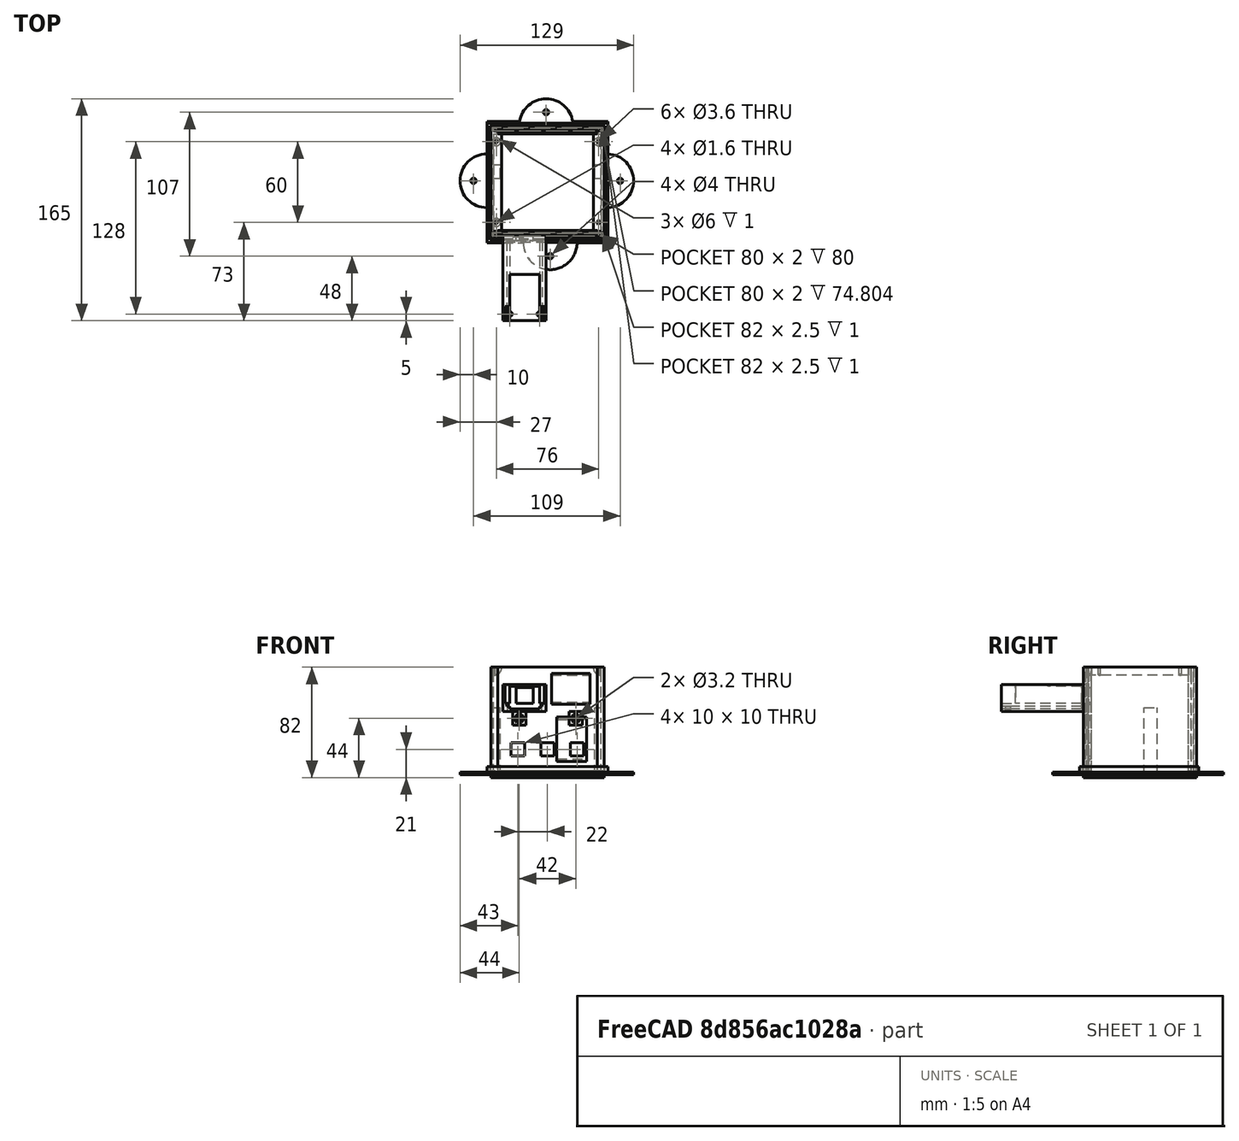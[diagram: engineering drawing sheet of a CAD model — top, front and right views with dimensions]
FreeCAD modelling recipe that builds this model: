
FCSTD DOCUMENT  (FreeCAD 0.19R24291 (Git))
Label: Project_ELE1
License: All rights reserved
LicenseURL: http://en.wikipedia.org/wiki/All_rights_reserved
objects: Part::Box×31, Part::Cylinder×25, Part::MultiFuse×9, Part::Cut×8, Part::Thickness×2, Part::FeaturePython×2, App::MeasureDistance×1
note: 77 computed .brp shape members not serialized (recipe doc carries the construction recipe); baked Part::Feature solids carry a one-line shape summary decoded from their .brp

FEATURE [Part::Box] Box  label="Cube"
  AttacherType = Attacher::AttachEngine3D
  Height = 80
  Length = 80
  Width = 80
FEATURE [Part::Thickness] Thickness
  Faces = -> Box [Face6]
  Intersection = false
  Join = 2
  Mode = 0
  SelfIntersection = false
  Value = 2
FEATURE [Part::Box] Box001  label="Cube001"
  AttacherType = Attacher::AttachEngine3D
  Height = 80
  Length = 80
  Placement = pos=(0,2,0) rot=(0,0,1;0rad)
  Width = 2
FEATURE [Part::Box] Box002  label="Cube002"
  AttacherType = Attacher::AttachEngine3D
  Height = 77
  Length = 74
  Placement = pos=(3,-4,3) rot=(0,0,1;0rad)
  Width = 8
FEATURE [Part::Cylinder] Cylinder
  Angle = 360
  AttacherType = Attacher::AttachEngine3D
  Height = 10
  Placement = pos=(2,10,70) rot=(0,0,1;0rad)
  Radius = 0.8
FEATURE [Part::Cylinder] Cylinder001
  Angle = 360
  AttacherType = Attacher::AttachEngine3D
  Height = 10
  Placement = pos=(2,70,70) rot=(0,0,1;0rad)
  Radius = 0.8
FEATURE [Part::Cylinder] Cylinder002
  Angle = 360
  AttacherType = Attacher::AttachEngine3D
  Height = 10
  Placement = pos=(78,70,70) rot=(0,0,1;0rad)
  Radius = 0.8
FEATURE [Part::Cylinder] Cylinder003
  Angle = 360
  AttacherType = Attacher::AttachEngine3D
  Height = 10
  Placement = pos=(78,10,70) rot=(0,0,1;0rad)
  Radius = 0.8
FEATURE [Part::Box] Box003  label="Cube003"
  AttacherType = Attacher::AttachEngine3D
  Height = 80
  Length = 80
  Placement = pos=(0,76,0) rot=(0,0,1;0rad)
  Width = 2
FEATURE [Part::Box] Box004  label="Cube004"
  AttacherType = Attacher::AttachEngine3D
  Height = 77
  Length = 74
  Placement = pos=(3,76,3) rot=(0,0,1;0rad)
  Width = 9
FEATURE [Part::MultiFuse] Fusion001
  Shapes = -> [Box002,Cylinder,Cylinder001,Cylinder002,Cylinder003,Box004]
FEATURE [Part::Cylinder] Cylinder004
  Angle = 90
  AttacherType = Attacher::AttachEngine3D
  Height = 74
  Placement = pos=(0,78,80) rot=(0.57735,0.57735,-0.57735;2.0944rad)
  Radius = 6
FEATURE [Part::Cylinder] Cylinder005
  Angle = 90
  AttacherType = Attacher::AttachEngine3D
  Height = 74
  Placement = pos=(80,78,80) rot=(0,0.707107,-0.707107;3.14159rad)
  Radius = 6
FEATURE [Part::Box] Box005  label="Cube005"
  AttacherType = Attacher::AttachEngine3D
  Height = 50
  Length = 5
  Placement = pos=(0,43,0) rot=(0,0,1;0rad)
  Width = 10
FEATURE [Part::Box] Box006  label="Cube006"
  AttacherType = Attacher::AttachEngine3D
  Height = 50
  Length = 5
  Placement = pos=(75,43,0) rot=(0,0,1;0rad)
  Width = 10
FEATURE [Part::MultiFuse] Fusion
  Shapes = -> [Box001,Thickness,Box003,Cylinder004,Cylinder005,Box005,Box006]
FEATURE [Part::Cut] Cut  label="Cut_obal"
  Base = -> Fusion
  Tool = -> Fusion001
FEATURE [Part::Box] Box007  label="Cube007"
  AttacherType = Attacher::AttachEngine3D
  Height = 77
  Length = 74
  Placement = pos=(3,1,3) rot=(0,0,1;0rad)
  Width = 2
FEATURE [Part::Box] Box008  label="Cube008"
  AttacherType = Attacher::AttachEngine3D
  Height = 79.5
  Length = 80
  Placement = pos=(0,2,0.5) rot=(0,0,1;0rad)
  Width = 1.5
FEATURE [Part::Cylinder] Cylinder006
  Angle = 360
  AttacherType = Attacher::AttachEngine3D
  Height = 10
  Placement = pos=(19,4,42) rot=(1,0,0;1.5708rad)
  Radius = 1.6
FEATURE [Part::Cylinder] Cylinder007
  Angle = 360
  AttacherType = Attacher::AttachEngine3D
  Height = 10
  Placement = pos=(61,5,42) rot=(1,0,0;1.5708rad)
  Radius = 1.6
FEATURE [Part::FeaturePython] Nut  label="(M3.5)-Nut"  # Fasteners workbench fastener (typed FeaturePython)
  Placement = pos=(19,1,42) rot=(1,0,0;1.5708rad)
  diameter = 5
  invert = false
  matchOuter = false
  offset = 0
  thread = false
  type = 9
FEATURE [Part::FeaturePython] Nut001  label="(M3.5)-Nut001"  # Fasteners workbench fastener (typed FeaturePython)
  Placement = pos=(61,1,42) rot=(1,0,0;1.5708rad)
  diameter = 5
  invert = false
  matchOuter = false
  offset = 0
  thread = false
  type = 9
FEATURE [Part::Box] Box009  label="Cube009"
  AttacherType = Attacher::AttachEngine3D
  Height = 10
  Length = 10
  Placement = pos=(14,-0.5,37) rot=(0,0,1;0rad)
  Width = 2
FEATURE [Part::Box] Box010  label="Cube010"
  AttacherType = Attacher::AttachEngine3D
  Height = 10
  Length = 10
  Placement = pos=(56,-0.5,37) rot=(0,0,1;0rad)
  Width = 4
FEATURE [Part::Box] Box012  label="Cube012"
  AttacherType = Attacher::AttachEngine3D
  Height = 10
  Length = 10
  Placement = pos=(13,0,14) rot=(0,0,1;0rad)
  Width = 10
FEATURE [Part::Box] Box013  label="Cube013"
  AttacherType = Attacher::AttachEngine3D
  Height = 10
  Length = 10
  Placement = pos=(57,0,14) rot=(0,0,1;0rad)
  Width = 10
FEATURE [Part::MultiFuse] Fusion003
  Shapes = -> [Box007,Box008,Box009,Box010]
FEATURE [Part::Box] Box014  label="Cube014"
  AttacherType = Attacher::AttachEngine3D
  Height = 79.5
  Length = 80
  Placement = pos=(0,2,0.5) rot=(0,0,1;0rad)
  Width = 1.5
FEATURE [Part::Box] Box015  label="Cube015"
  AttacherType = Attacher::AttachEngine3D
  Height = 77
  Length = 74
  Placement = pos=(3,1,3) rot=(0,0,1;0rad)
  Width = 2
FEATURE [Part::Box] Box018  label="Vypinac"
  AttacherType = Attacher::AttachEngine3D
  Height = 29
  Length = 22
  Placement = pos=(47,-6.5,12) rot=(0,0,1;0rad)
  Width = 10
FEATURE [Part::Box] Box019  label="PC"
  AttacherType = Attacher::AttachEngine3D
  Height = 20
  Length = 28.5
  Placement = pos=(43,0,54) rot=(0,0,1;0rad)
  Width = 10
FEATURE [Part::Box] Box020  label="Vypinac001"
  AttacherType = Attacher::AttachEngine3D
  Height = 33
  Length = 22
  Placement = pos=(47,-7.5,10) rot=(0,0,1;0rad)
  Width = 10
FEATURE [Part::Box] Box021  label="PC001"
  AttacherType = Attacher::AttachEngine3D
  Height = 23
  Length = 28.5
  Placement = pos=(43,-7.3,52.5) rot=(0,0,1;0rad)
  Width = 10
FEATURE [Part::Box] Box022  label="Cube016_USB"
  AttacherType = Attacher::AttachEngine3D
  Height = 12
  Length = 12.6
  Placement = pos=(16.7,-9,53) rot=(0,0,1;0rad)
  Width = 20
FEATURE [Part::Box] Box023  label="Cube017_rele"
  AttacherType = Attacher::AttachEngine3D
  Height = 20
  Length = 32
  Placement = pos=(39,1,47) rot=(0,0,1;3.14159rad)
  Width = 64
FEATURE [Part::MultiFuse] Fusion005
  Shapes = -> [Box015,Box014,Box023]
FEATURE [Part::Box] Box024  label="Cube018_doska"
  AttacherType = Attacher::AttachEngine3D
  Height = 2.2
  Length = 26.2
  Placement = pos=(35.9,-3.5,51) rot=(0,0,1;3.14159rad)
  Width = 60
FEATURE [Part::Box] Box025  label="Cube019_okolo_doskjy"
  AttacherType = Attacher::AttachEngine3D
  Height = 17
  Length = 22
  Placement = pos=(34,-3.5,49) rot=(0,0,1;3.14159rad)
  Width = 60
FEATURE [Part::Cylinder] Cylinder008
  Angle = 360
  AttacherType = Attacher::AttachEngine3D
  Height = 30
  Placement = pos=(34,-58,38) rot=(0,0,1;0rad)
  Radius = 1.8
FEATURE [Part::Cylinder] Cylinder009
  Angle = 360
  AttacherType = Attacher::AttachEngine3D
  Height = 30
  Placement = pos=(12,-58,38) rot=(0,0,1;0rad)
  Radius = 1.8
FEATURE [Part::Box] Box026  label="Cube016_pre_sroby"
  AttacherType = Attacher::AttachEngine3D
  Height = 15
  Length = 29
  Placement = pos=(8.5,-65.5,53.2) rot=(0,0,1;0rad)
  Width = 13
FEATURE [Part::Box] Box027  label="Cube016_pre_rele"
  AttacherType = Attacher::AttachEngine3D
  Height = 15
  Length = 22
  Placement = pos=(12,-53.5,65.2) rot=(0,0,1;0rad)
  Width = 25
FEATURE [Part::MultiFuse] Fusion006  label="Fusion006_usbrele"
  Shapes = -> [Box022,Box024,Box025,Cylinder008,Cylinder009,Box026,Box027]
FEATURE [Part::MultiFuse] Fusion004
  Shapes = -> [Box018,Box019,Box020,Box021,Fusion006]
FEATURE [Part::Cut] Cut002  label="Cut_zadok_usb"
  Base = -> Fusion005
  Tool = -> Fusion004
FEATURE [Part::Box] Box028  label="Cube016"
  AttacherType = Attacher::AttachEngine3D
  Height = 10
  Length = 10
  Placement = pos=(35,0,14) rot=(0,0,1;0rad)
  Width = 10
FEATURE [Part::MultiFuse] Fusion002
  Shapes = -> [Cylinder006,Cylinder007,Nut,Nut001,Box013,Box012,Box028]
FEATURE [Part::Cut] Cut001  label="Cut_predok"
  Base = -> Fusion003
  Tool = -> Fusion002
FEATURE [Part::Box] Box029  label="Cube017"
  AttacherType = Attacher::AttachEngine3D
  Height = 2
  Length = 90
  Placement = pos=(-5,-5,0) rot=(0,0,1;0rad)
  Width = 90
FEATURE [Part::Box] Box030  label="Cube018"
  AttacherType = Attacher::AttachEngine3D
  Height = 1
  Length = 82
  Placement = pos=(-1,0,1) rot=(0,0,1;0rad)
  Width = 2.5
FEATURE [Part::Cylinder] Cylinder012
  Angle = 360
  AttacherType = Attacher::AttachEngine3D
  Height = 300
  Placement = pos=(78,10,-70) rot=(0,0,1;0rad)
  Radius = 1.8
FEATURE [Part::Cylinder] Cylinder013
  Angle = 360
  AttacherType = Attacher::AttachEngine3D
  Height = 300
  Placement = pos=(78,70,-107) rot=(0,0,1;0rad)
  Radius = 1.8
FEATURE [Part::Cylinder] Cylinder014
  Angle = 360
  AttacherType = Attacher::AttachEngine3D
  Height = 300
  Placement = pos=(2,10,-63) rot=(0,0,1;0rad)
  Radius = 1.8
FEATURE [Part::Cylinder] Cylinder015
  Angle = 360
  AttacherType = Attacher::AttachEngine3D
  Height = 300
  Placement = pos=(2,70,-69) rot=(0,0,1;0rad)
  Radius = 1.8
FEATURE [Part::Box] Box034  label="Cube022"
  AttacherType = Attacher::AttachEngine3D
  Height = 1
  Length = 82
  Placement = pos=(-1,78,1) rot=(0,0,1;0rad)
  Width = 2.5
FEATURE [Part::Box] Box035  label="Cube023"
  AttacherType = Attacher::AttachEngine3D
  Height = 2
  Length = 84
  Placement = pos=(-2,-4,1) rot=(0,0,1;0rad)
  Width = 2
FEATURE [Part::Box] Box038  label="Cube026"
  AttacherType = Attacher::AttachEngine3D
  Height = 4
  Length = 85.6
  Placement = pos=(-2.8,-2.8,2) rot=(0,0,1;0rad)
  Width = 84.6
FEATURE [Part::Thickness] Thickness001
  Faces = -> Box038 [Face5,Face6]
  Intersection = false
  Join = 2
  Mode = 0
  SelfIntersection = false
  Value = 2
FEATURE [Part::Cylinder] Cylinder016
  Angle = 360
  AttacherType = Attacher::AttachEngine3D
  Height = 1
  Placement = pos=(2,10,0) rot=(0,0,1;0rad)
  Radius = 3
FEATURE [Part::Cylinder] Cylinder017
  Angle = 360
  AttacherType = Attacher::AttachEngine3D
  Height = 1
  Placement = pos=(2,70,0) rot=(0,0,1;0rad)
  Radius = 3
FEATURE [Part::Cylinder] Cylinder018
  Angle = 360
  AttacherType = Attacher::AttachEngine3D
  Height = 1
  Placement = pos=(78,70,0) rot=(0,0,1;0rad)
  Radius = 3
FEATURE [Part::MultiFuse] Fusion008
  Shapes = -> [Cylinder014,Cylinder015,Cylinder013,Cylinder012,Box034,Box030,Cylinder016,Cylinder017,Cylinder018]
FEATURE [Part::Cylinder] Cylinder020
  Angle = 360
  AttacherType = Attacher::AttachEngine3D
  Height = 2
  Placement = pos=(-5,41,0) rot=(0,0,1;0rad)
  Radius = 20
FEATURE [Part::Cylinder] Cylinder021
  Angle = 360
  AttacherType = Attacher::AttachEngine3D
  Height = 2
  Placement = pos=(84,41,0) rot=(0,0,1;0rad)
  Radius = 20
FEATURE [Part::Cylinder] Cylinder022
  Angle = 360
  AttacherType = Attacher::AttachEngine3D
  Height = 10
  Placement = pos=(94,41,0) rot=(0,0,1;0rad)
  Radius = 2
FEATURE [Part::Cut] Cut004
  Base = -> Cylinder021
  Tool = -> Cylinder022
FEATURE [Part::Cylinder] Cylinder023
  Angle = 360
  AttacherType = Attacher::AttachEngine3D
  Height = 10
  Placement = pos=(-15,41,0) rot=(0,0,1;0rad)
  Radius = 2
FEATURE [Part::Cut] Cut005
  Base = -> Cylinder020
  Tool = -> Cylinder023
FEATURE [Part::Cylinder] Cylinder024
  Angle = 360
  AttacherType = Attacher::AttachEngine3D
  Height = 10
  Placement = pos=(-15,41,0) rot=(0,0,1;0rad)
  Radius = 2
FEATURE [Part::Cylinder] Cylinder025
  Angle = 180
  AttacherType = Attacher::AttachEngine3D
  Height = 2
  Placement = pos=(-5,41,0) rot=(0,0,1;1.5708rad)
  Radius = 20
FEATURE [Part::Cut] Cut006
  Base = -> Cylinder025
  Placement = pos=(83,-1.2e-14,0) rot=(0,0,1;1.5708rad)
  Tool = -> Cylinder024
FEATURE [Part::Cylinder] Cylinder026
  Angle = 360
  AttacherType = Attacher::AttachEngine3D
  Height = 10
  Placement = pos=(-15,41,0) rot=(0,0,1;0rad)
  Radius = 2
FEATURE [Part::Cylinder] Cylinder027
  Angle = 180
  AttacherType = Attacher::AttachEngine3D
  Height = 2
  Placement = pos=(-5,41,0) rot=(0,0,1;1.5708rad)
  Radius = 20
FEATURE [Part::Cut] Cut007
  Base = -> Cylinder027
  Placement = pos=(-2,77,0) rot=(0,0,-1;1.5708rad)
  Tool = -> Cylinder026
FEATURE [Part::MultiFuse] Fusion007
  Shapes = -> [Box029,Box035,Thickness001,Cut004,Cut005,Cut007,Cut006]
FEATURE [Part::Cut] Cut003  label="Cut_vrch"
  Base = -> Fusion007
  Tool = -> Fusion008
FEATURE [App::MeasureDistance] Distance  label="Distance: 84.77 mm"
  Distance = 84.7706
  P1 = (82.205,82.3,6)
  P2 = (-2.56551,82.2822,6)
